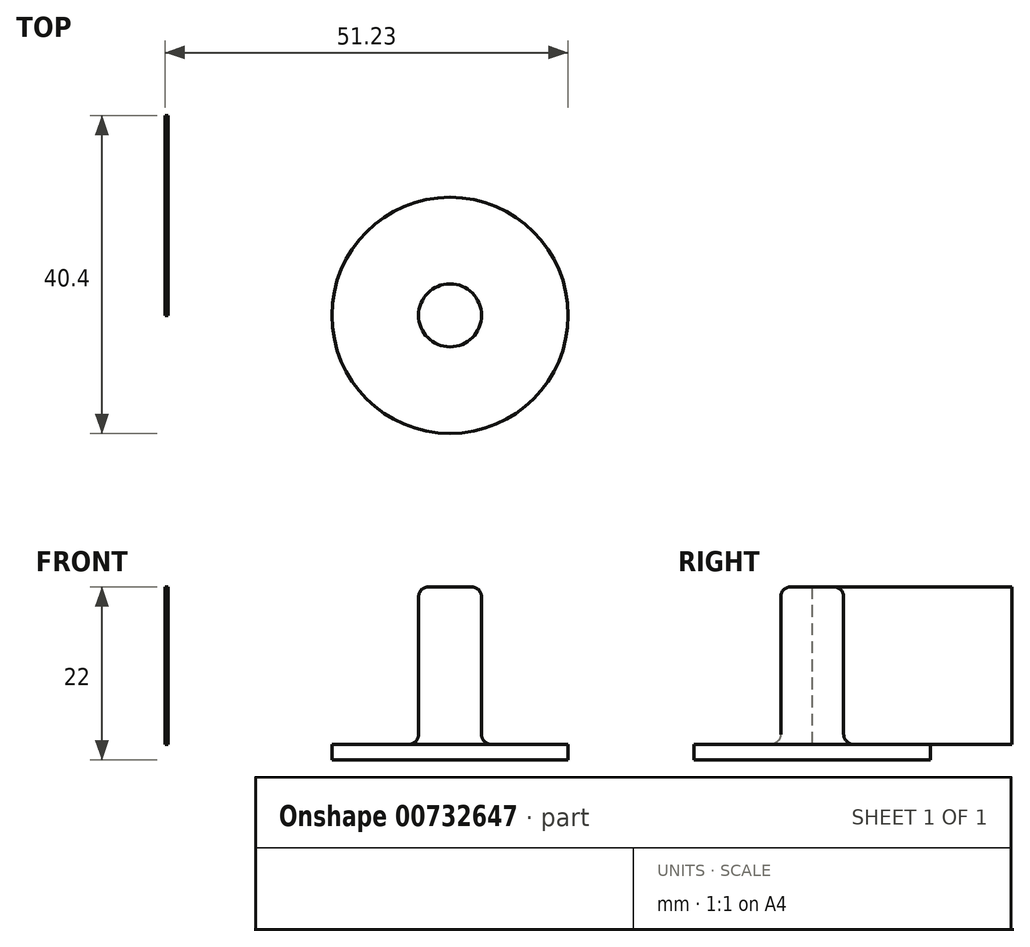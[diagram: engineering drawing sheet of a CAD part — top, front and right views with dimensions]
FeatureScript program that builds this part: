
annotation { "Feature Type Name" : "Feature", "Feature Type Description" : "" }
export const myFeature = defineFeature(function(context is Context, id is Id, definition is map)
    precondition{}
    {
        {
            var Q0;
            Q0=qCreatedBy(makeId("Front.planeOp"),FACE);
            var sketch = newSketch(context, id + "F0", { "sketchPlane" : qUnion([Q0])});
            skLineSegment(sketch, "E0.bottom", {"start": v(0, 0) * mm, "end": v(-4, 0) * mm});
            skLineSegment(sketch, "E0.top", {"start": v(0, 20) * mm, "end": v(-4, 20) * mm});
            skLineSegment(sketch, "E0.left", {"start": v(0, 0) * mm, "end": v(0, 20) * mm});
            skLineSegment(sketch, "E0.right", {"start": v(-4, 0) * mm, "end": v(-4, 20) * mm});
            skLineSegment(sketch, "E1.bottom", {"start": v(0, 0) * mm, "end": v(-15, 0) * mm});
            skLineSegment(sketch, "E1.top", {"start": v(0, -2) * mm, "end": v(-15, -2) * mm});
            skLineSegment(sketch, "E1.left", {"start": v(0, 0) * mm, "end": v(0, -2) * mm});
            skLineSegment(sketch, "E1.right", {"start": v(-15, 0) * mm, "end": v(-15, -2) * mm});
            skSolve(sketch);
        }
        {
            var Q0;
            Q0 = qSketchRegion(id + "F0", true);
            var Q1;
            Q1=sQuery(id+"F0.wireOp",EDGE,"E0.left");
            revolve(context, id + "F1", {"surfaceOperationType" : NewSurfaceOperationType.NEW, "entities" : qUnion([Q0]), "axis" : qUnion([Q1]), "revolveType" : RevolveType.FULL});
        }
        {
            var Q0;
            Q0=makeQuery(id+"F1.opRevolve","SWEPT_EDGE",EDGE,{"disambiguationData":[OSD([sQuery(id+"F0.wireOp",EDGE,"E0.top"),sQuery(id+"F0.wireOp",EDGE,"E0.right")])]});
            var Q1;
            Q1=makeQuery(id+"F1.opRevolve","SWEPT_EDGE",EDGE,{"disambiguationData":[OSD([sQuery(id+"F0.wireOp",EDGE,"E0.right"),sQuery(id+"F0.wireOp",EDGE,"E1.bottom")])]});
            fillet(context, id + "F2", {"entities" : qUnion([Q0, Q1]), "radius" : 1.27 * mm, "tangentPropagation" : true, "allowEdgeOverflow" : false});
        }
        {
            var Q0;
            Q0=qCreatedBy(makeId("Top.planeOp"),FACE);
            var sketch = newSketch(context, id + "F3", { "sketchPlane" : qUnion([Q0])});
            skLineSegment(sketch, "E2", {"start": v(-36.23, 25.4) * mm, "end": v(-36.23, 0) * mm});
            skLineSegment(sketch, "E3", {"start": v(-36.23, 0) * mm, "end": v(-35.83, 0) * mm});
            skLineSegment(sketch, "E4", {"start": v(-35.83, 0) * mm, "end": v(-35.83, 25.4) * mm});
            skLineSegment(sketch, "E5", {"start": v(-35.83, 25.4) * mm, "end": v(-36.23, 25.4) * mm});
            skSolve(sketch);
        }
        {
            var Q0;
            Q0=makeQuery(id+"F3.imprint","IMPRINT",FACE,{"disambiguationData":[TD([[makeQuery(id+"F3.imprint","IMPRINT",EDGE,{"derivedFrom":sQuery(id+"F3.wireOp",EDGE,"E2")}),1.0]])]});
            extrude(context, id + "F4", {"entities" : qUnion([Q0]), "depth" : 19.99 * mm, "offsetDistance" : 25.4 * mm});
        }
    });
